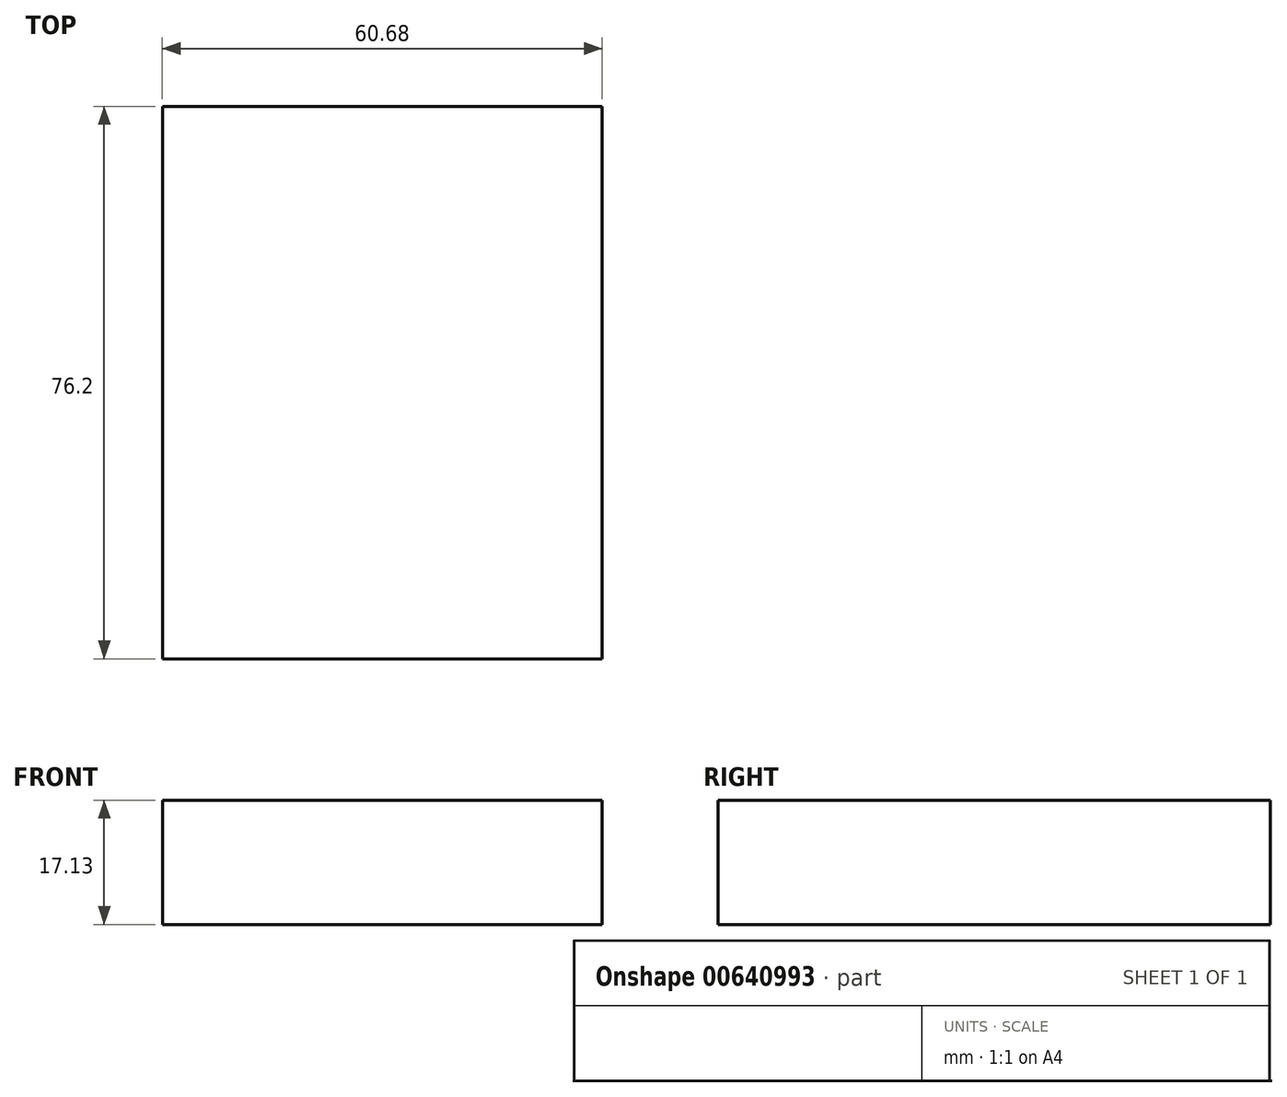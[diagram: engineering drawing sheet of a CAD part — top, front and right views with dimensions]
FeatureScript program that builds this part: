
annotation { "Feature Type Name" : "Feature", "Feature Type Description" : "" }
export const myFeature = defineFeature(function(context is Context, id is Id, definition is map)
    precondition{}
    {
        {
            var Q0;
            Q0=qCreatedBy(makeId("Front.planeOp"),FACE);
            var sketch = newSketch(context, id + "F0", { "sketchPlane" : qUnion([Q0])});
            skLineSegment(sketch, "E0.bottom", {"start": v(0, 0) * mm, "end": v(-60.68, 0) * mm});
            skLineSegment(sketch, "E0.top", {"start": v(0, 17.13) * mm, "end": v(-60.68, 17.13) * mm});
            skLineSegment(sketch, "E0.left", {"start": v(0, 0) * mm, "end": v(0, 17.13) * mm});
            skLineSegment(sketch, "E0.right", {"start": v(-60.68, 0) * mm, "end": v(-60.68, 17.13) * mm});
            skPoint(sketch, "E0.middle", {"position": v(-30.34, 8.56) * mm});
            skLineSegment(sketch, "E1.bottom", {"start": v(35.2, 57.76) * mm, "end": v(-0.11, 57.76) * mm});
            skLineSegment(sketch, "E1.top", {"start": v(35.2, 67.03) * mm, "end": v(-0.11, 67.03) * mm});
            skLineSegment(sketch, "E1.left", {"start": v(35.2, 57.76) * mm, "end": v(35.2, 67.03) * mm});
            skLineSegment(sketch, "E1.right", {"start": v(-0.11, 57.76) * mm, "end": v(-0.11, 67.03) * mm});
            skPoint(sketch, "E1.middle", {"position": v(17.54, 62.4) * mm});
            skSolve(sketch);
        }
        {
            var Q0;
            Q0=makeQuery(id+"F0.imprint","IMPRINT",FACE,{"disambiguationData":[TD([[makeQuery(id+"F0.imprint","IMPRINT",EDGE,{"derivedFrom":sQuery(id+"F0.wireOp",EDGE,"E0.bottom")}),-1.0]])]});
            extrude(context, id + "F1", {"entities" : qUnion([Q0]), "depth" : 76.2 * mm, "offsetDistance" : 25.4 * mm});
        }
    });
